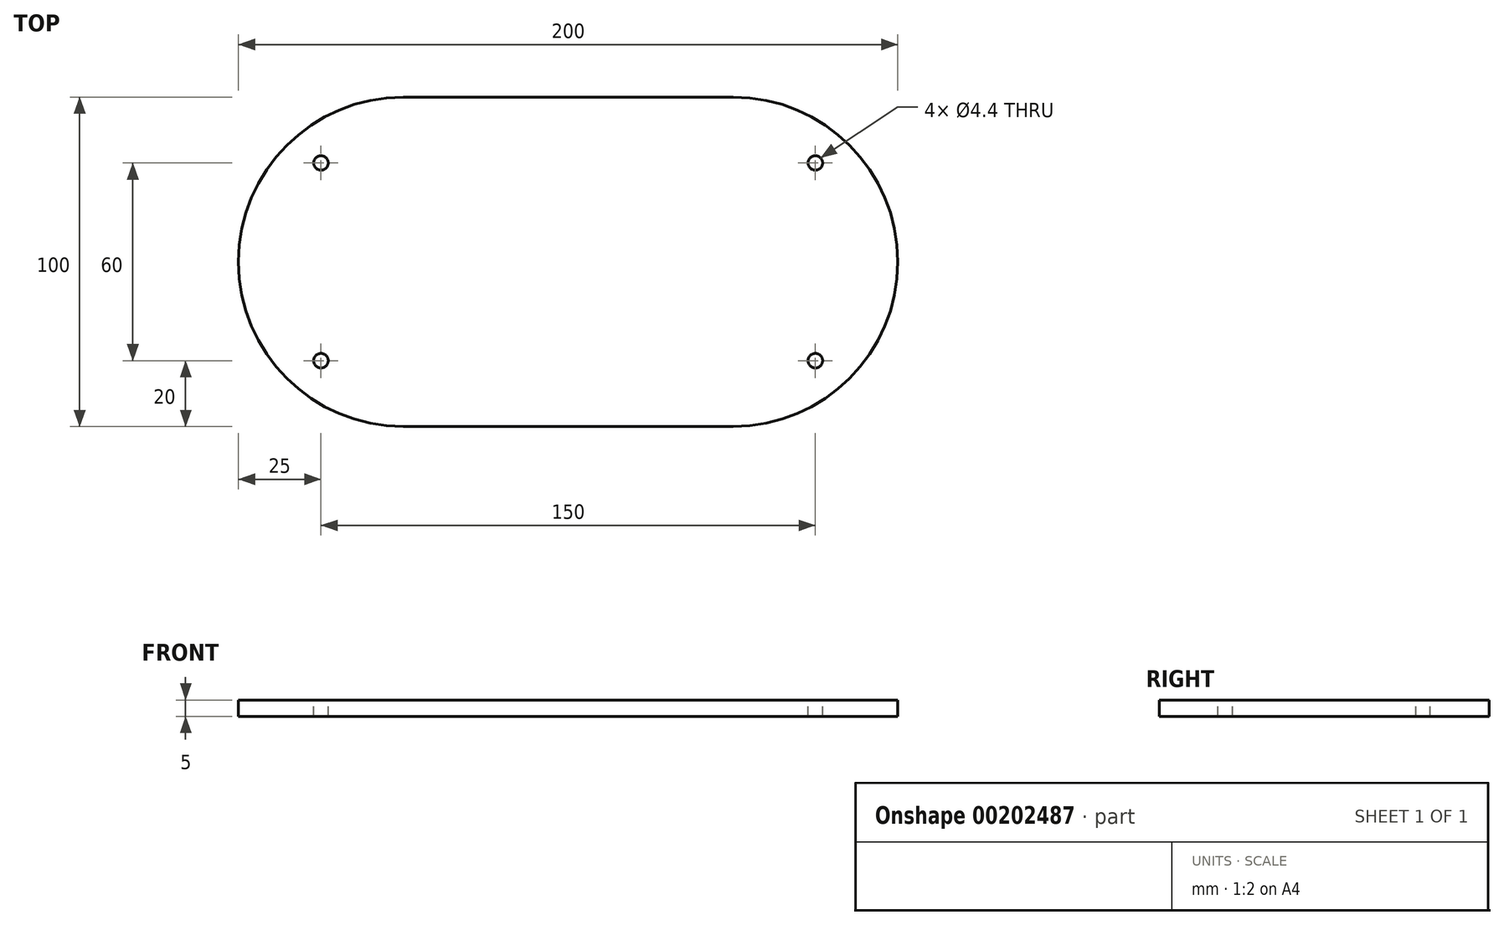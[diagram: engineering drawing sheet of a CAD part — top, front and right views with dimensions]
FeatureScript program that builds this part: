
annotation { "Feature Type Name" : "Feature", "Feature Type Description" : "" }
export const myFeature = defineFeature(function(context is Context, id is Id, definition is map)
    precondition{}
    {
        {
            var Q0;
            Q0=qCreatedBy(makeId("Top.planeOp"),FACE);
            var sketch = newSketch(context, id + "F0", { "sketchPlane" : qUnion([Q0])});
            skLineSegment(sketch, "E0.bottom", {"start": v(50, 50) * mm, "end": v(-50, 50) * mm});
            skLineSegment(sketch, "E0.top", {"start": v(50, -50) * mm, "end": v(-50, -50) * mm});
            skLineSegment(sketch, "E0.left", {"start": v(50, 50) * mm, "end": v(50, -50) * mm});
            skLineSegment(sketch, "E0.right", {"start": v(-50, 50) * mm, "end": v(-50, -50) * mm});
            skPoint(sketch, "E0.middle", {"position": v(0, 0) * mm});
            skArc(sketch, "E1", {"start": v(-50, 50) * mm, "mid": v(-100, 0) * mm, "end": v(-50, -50) * mm});
            skArc(sketch, "E2", {"start": v(-50, -50) * mm, "mid": v(0, 0) * mm, "end": v(-50, 50) * mm, "construction": true});
            skArc(sketch, "E3", {"start": v(50, 50) * mm, "mid": v(0, 0) * mm, "end": v(50, -50) * mm, "construction": true});
            skArc(sketch, "E4", {"start": v(50, -50) * mm, "mid": v(100, 0) * mm, "end": v(50, 50) * mm});
            skSolve(sketch);
        }
        {
            var Q0;
            Q0 = qSketchRegion(id + "F0", true);
            extrude(context, id + "F1", {"entities" : qUnion([Q0]), "depth" : 5 * mm});
        }
        {
            var Q0;
            Q0=makeQuery(id+"F1.opExtrude","CAP_FACE",FACE,{"disambiguationData":[OSD([sQuery(id+"F0.wireOp",EDGE,"E0.bottom"),sQuery(id+"F0.wireOp",EDGE,"E0.top"),sQuery(id+"F0.wireOp",EDGE,"E1"),sQuery(id+"F0.wireOp",EDGE,"E4")])],"isStart":false});
            var sketch = newSketch(context, id + "F2", { "sketchPlane" : qUnion([Q0])});
            skLineSegment(sketch, "E5.bottom", {"start": v(75, 30) * mm, "end": v(-75, 30) * mm, "construction": true});
            skLineSegment(sketch, "E5.top", {"start": v(75, -30) * mm, "end": v(-75, -30) * mm, "construction": true});
            skLineSegment(sketch, "E5.left", {"start": v(75, 30) * mm, "end": v(75, -30) * mm, "construction": true});
            skLineSegment(sketch, "E5.right", {"start": v(-75, 30) * mm, "end": v(-75, -30) * mm, "construction": true});
            skPoint(sketch, "E5.middle", {"position": v(0, 0) * mm});
            skPoint(sketch, "E6", {"position": v(-75, 30) * mm});
            skPoint(sketch, "E7", {"position": v(75, 30) * mm});
            skPoint(sketch, "E8", {"position": v(75, -30) * mm});
            skPoint(sketch, "E9", {"position": v(-75, -30) * mm});
            skSolve(sketch);
        }
        {
            var Q0;
            Q0=sQuery(id+"F2.wireOp",VERTEX,"E6");
            var Q1;
            Q1=sQuery(id+"F2.wireOp",VERTEX,"E7");
            var Q2;
            Q2=sQuery(id+"F2.wireOp",VERTEX,"E8");
            var Q3;
            Q3=sQuery(id+"F2.wireOp",VERTEX,"E9");
            var Q4;
            Q4=makeQuery(id+"F1.opExtrude","SWEPT_BODY",BODY,{"disambiguationData":[OSD([sQuery(id+"F0.wireOp",EDGE,"E0.bottom"),sQuery(id+"F0.wireOp",EDGE,"E0.top"),sQuery(id+"F0.wireOp",EDGE,"E1"),sQuery(id+"F0.wireOp",EDGE,"E4")])]});
            hole(context, id + "F3", {"style" : HoleStyle.SIMPLE, "endStyle" : HoleEndStyle.THROUGH, "standardTappedOrClearance" : lookupTablePath({ "standard" : "ISO", "fit" : "Normal", "size" : "M4", "type" : "Clearance" }), "standardBlindInLast" : lookupTablePath({ "fit" : "Standard", "standard" : "ISO", "size" : "M4", "type" : "Clearance" }), "holeDiameter" : 4.4 * mm, "locations" : qUnion([Q0, Q1, Q2, Q3]), "scope" : qUnion([Q4]), "isTappedThrough" : true});
        }
    });
